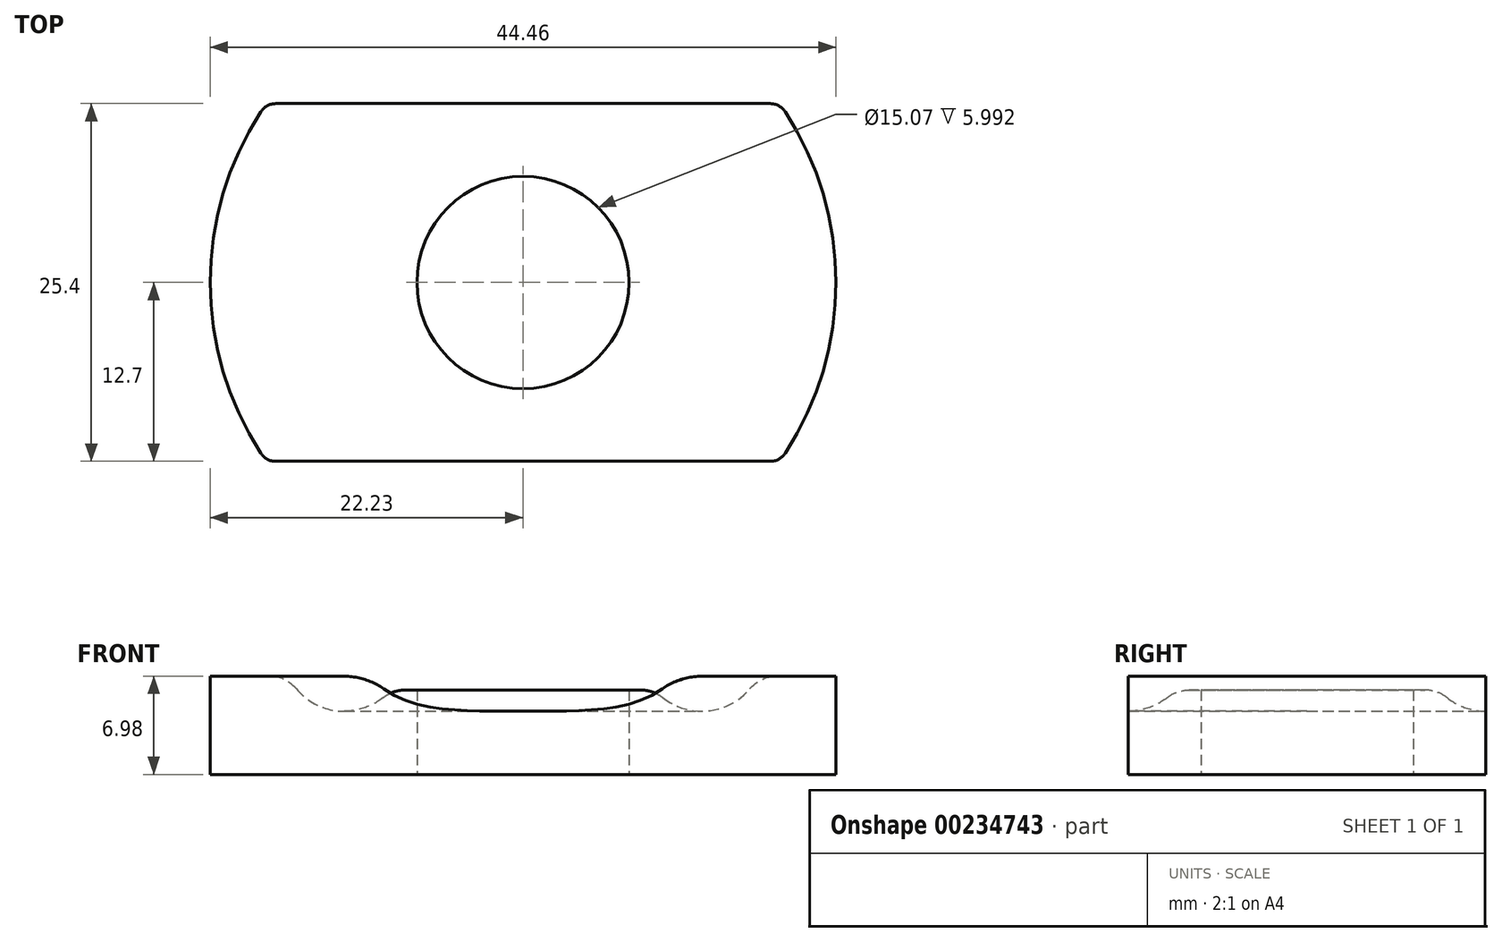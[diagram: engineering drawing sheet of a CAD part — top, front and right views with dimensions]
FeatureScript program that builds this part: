
annotation { "Feature Type Name" : "Feature", "Feature Type Description" : "" }
export const myFeature = defineFeature(function(context is Context, id is Id, definition is map)
    precondition{}
    {
        {
            var Q0;
            Q0=qCreatedBy(makeId("Top.planeOp"),FACE);
            var sketch = newSketch(context, id + "F0", { "sketchPlane" : qUnion([Q0])});
            skArc(sketch, "E0", {"start": v(-18.24, 12.7) * mm, "mid": v(-22.23, 0) * mm, "end": v(-18.24, -12.7) * mm});
            skLineSegment(sketch, "E1.bottom", {"start": v(18.24, 12.7) * mm, "end": v(-18.24, 12.7) * mm});
            skLineSegment(sketch, "E1.top", {"start": v(18.24, -12.7) * mm, "end": v(-18.24, -12.7) * mm});
            skLineSegment(sketch, "E1.left", {"start": v(18.24, 12.7) * mm, "end": v(18.24, -12.7) * mm, "construction": true});
            skLineSegment(sketch, "E1.right", {"start": v(-18.24, 12.7) * mm, "end": v(-18.24, -12.7) * mm, "construction": true});
            skArc(sketch, "E2.trimOffspring", {"start": v(18.24, -12.7) * mm, "mid": v(22.23, 0) * mm, "end": v(18.24, 12.7) * mm});
            skCircle(sketch, "E3", {"center": v(0, 0) * mm, "radius": 7.54 * mm});
            skSolve(sketch);
        }
        {
            var Q0;
            Q0=qSketchRegion(id+"F0",true);
            extrude(context, id + "F1", {"entities" : qUnion([Q0]), "endBound" : BoundingType.SYMMETRIC, "depth" : 7 * mm});
        }
        {
            var Q0;
            Q0=qCreatedBy(makeId("Front.planeOp"),FACE);
            var sketch = newSketch(context, id + "F2", { "sketchPlane" : qUnion([Q0])});
            skCircle(sketch, "E4", {"center": v(12.7, 5.45) * mm, "radius": 4.45 * mm});
            skLineSegment(sketch, "E5", {"start": v(12.7, 5.45) * mm, "end": v(12.7, 3.5) * mm});
            skLineSegment(sketch, "E6", {"start": v(12.7, 3.5) * mm, "end": v(12.7, 1) * mm});
            skLineSegment(sketch, "E7", {"start": v(10.64, 9.38) * mm, "end": v(0, 9.38) * mm});
            skLineSegment(sketch, "E8", {"start": v(0, 9.38) * mm, "end": v(0, 2.5) * mm});
            skLineSegment(sketch, "E9", {"start": v(0, 2.5) * mm, "end": v(16.03, 2.5) * mm});
            skLineSegment(sketch, "E10", {"start": v(0, 0) * mm, "end": v(-5.27, 0) * mm, "construction": true});
            skSolve(sketch);
        }
        {
            var Q0;
            Q0=qSketchRegion(id+"F2",true);
            var Q1;
            Q1=makeQuery(id+"F1.opExtrude","SWEPT_FACE",FACE,{"disambiguationData":[OSD([sQuery(id+"F0.wireOp",EDGE,"E3")])]});
            revolve(context, id + "F3", {"operationType" : NewBodyOperationType.REMOVE, "entities" : qUnion([Q0]), "axis" : qUnion([Q1]), "revolveType" : RevolveType.FULL, "oppositeDirection" : true});
        }
        {
            var Q0;
            Q0=makeQuery(id+"F3.boolean.opBoolean","INTERSECT",EDGE,{"disambiguationData":[OD(1.0)],"derivedFrom":[makeQuery(id+"F1.opExtrude","CAP_FACE",FACE,{"disambiguationData":[OSD([sQuery(id+"F0.wireOp",EDGE,"E0"),sQuery(id+"F0.wireOp",EDGE,"E1.bottom"),sQuery(id+"F0.wireOp",EDGE,"E1.top"),sQuery(id+"F0.wireOp",EDGE,"E2.trimOffspring"),sQuery(id+"F0.wireOp",EDGE,"E3")])],"isStart":false}),makeQuery(id+"F3.opRevolve","SWEPT_FACE",FACE,{"disambiguationData":[OSD([sQuery(id+"F2.wireOp",EDGE,"E4")])]})]});
            var Q1;
            Q1=makeQuery(id+"F3.boolean.opBoolean","INTERSECT",EDGE,{"disambiguationData":[OD(0.0)],"derivedFrom":[makeQuery(id+"F1.opExtrude","CAP_FACE",FACE,{"disambiguationData":[OSD([sQuery(id+"F0.wireOp",EDGE,"E0"),sQuery(id+"F0.wireOp",EDGE,"E1.bottom"),sQuery(id+"F0.wireOp",EDGE,"E1.top"),sQuery(id+"F0.wireOp",EDGE,"E2.trimOffspring"),sQuery(id+"F0.wireOp",EDGE,"E3")])],"isStart":false}),makeQuery(id+"F3.opRevolve","SWEPT_FACE",FACE,{"disambiguationData":[OSD([sQuery(id+"F2.wireOp",EDGE,"E4")])]})]});
            var Q2;
            Q2=makeQuery(id+"F3.boolean.opBoolean","COPY",EDGE,{"derivedFrom":makeQuery(id+"F3.opRevolve","SWEPT_EDGE",EDGE,{"disambiguationData":[OSD([sQuery(id+"F2.wireOp",EDGE,"E4"),sQuery(id+"F2.wireOp",EDGE,"E9")])]})});
            var Q3;
            Q3=makeQuery(id+"FBVG78wqvWEtJCH_1.1.F3.boolean.opBoolean","INTERSECT",EDGE,{"disambiguationData":[OD(1.0)],"derivedFrom":[makeQuery(id+"F1.opExtrude","CAP_FACE",FACE,{"disambiguationData":[OSD([sQuery(id+"F0.wireOp",EDGE,"E0"),sQuery(id+"F0.wireOp",EDGE,"E1.bottom"),sQuery(id+"F0.wireOp",EDGE,"E1.top"),sQuery(id+"F0.wireOp",EDGE,"E2.trimOffspring"),sQuery(id+"F0.wireOp",EDGE,"E3")])],"isStart":true}),makeQuery(id+"FBVG78wqvWEtJCH_1.1.F3.opRevolve","SWEPT_FACE",FACE,{"disambiguationData":[OSD([sQuery(id+"F2.wireOp",EDGE,"E4")])]})]});
            var Q4;
            Q4=makeQuery(id+"FBVG78wqvWEtJCH_1.1.F3.boolean.opBoolean","COPY",EDGE,{"derivedFrom":makeQuery(id+"FBVG78wqvWEtJCH_1.1.F3.opRevolve","SWEPT_EDGE",EDGE,{"disambiguationData":[OSD([sQuery(id+"F2.wireOp",EDGE,"E4"),sQuery(id+"F2.wireOp",EDGE,"E9")])]})});
            var Q5;
            Q5=makeQuery(id+"FBVG78wqvWEtJCH_1.1.F3.boolean.opBoolean","INTERSECT",EDGE,{"disambiguationData":[OD(0.0)],"derivedFrom":[makeQuery(id+"F1.opExtrude","CAP_FACE",FACE,{"disambiguationData":[OSD([sQuery(id+"F0.wireOp",EDGE,"E0"),sQuery(id+"F0.wireOp",EDGE,"E1.bottom"),sQuery(id+"F0.wireOp",EDGE,"E1.top"),sQuery(id+"F0.wireOp",EDGE,"E2.trimOffspring"),sQuery(id+"F0.wireOp",EDGE,"E3")])],"isStart":true}),makeQuery(id+"FBVG78wqvWEtJCH_1.1.F3.opRevolve","SWEPT_FACE",FACE,{"disambiguationData":[OSD([sQuery(id+"F2.wireOp",EDGE,"E4")])]})]});
            fillet(context, id + "F4", {"entities" : qUnion([Q0, Q1, Q2, Q3, Q4, Q5]), "radius" : 2.54 * mm, "tangentPropagation" : true, "allowEdgeOverflow" : false});
        }
        {
            var Q0;
            Q0=makeQuery(id+"F1.opExtrude","SWEPT_EDGE",EDGE,{"disambiguationData":[OSD([sQuery(id+"F0.wireOp",EDGE,"E0"),sQuery(id+"F0.wireOp",EDGE,"E1.top")])]});
            var Q1;
            Q1=makeQuery(id+"F1.opExtrude","SWEPT_EDGE",EDGE,{"disambiguationData":[OSD([sQuery(id+"F0.wireOp",EDGE,"E1.top"),sQuery(id+"F0.wireOp",EDGE,"E2.trimOffspring")])]});
            var Q2;
            Q2=makeQuery(id+"F1.opExtrude","SWEPT_EDGE",EDGE,{"disambiguationData":[OSD([sQuery(id+"F0.wireOp",EDGE,"E0"),sQuery(id+"F0.wireOp",EDGE,"E1.bottom")])]});
            var Q3;
            Q3=makeQuery(id+"F1.opExtrude","SWEPT_EDGE",EDGE,{"disambiguationData":[OSD([sQuery(id+"F0.wireOp",EDGE,"E1.bottom"),sQuery(id+"F0.wireOp",EDGE,"E2.trimOffspring")])]});
            fillet(context, id + "F5", {"entities" : qUnion([Q0, Q1, Q2, Q3]), "radius" : 1.27 * mm, "tangentPropagation" : true, "allowEdgeOverflow" : false});
        }
    });
